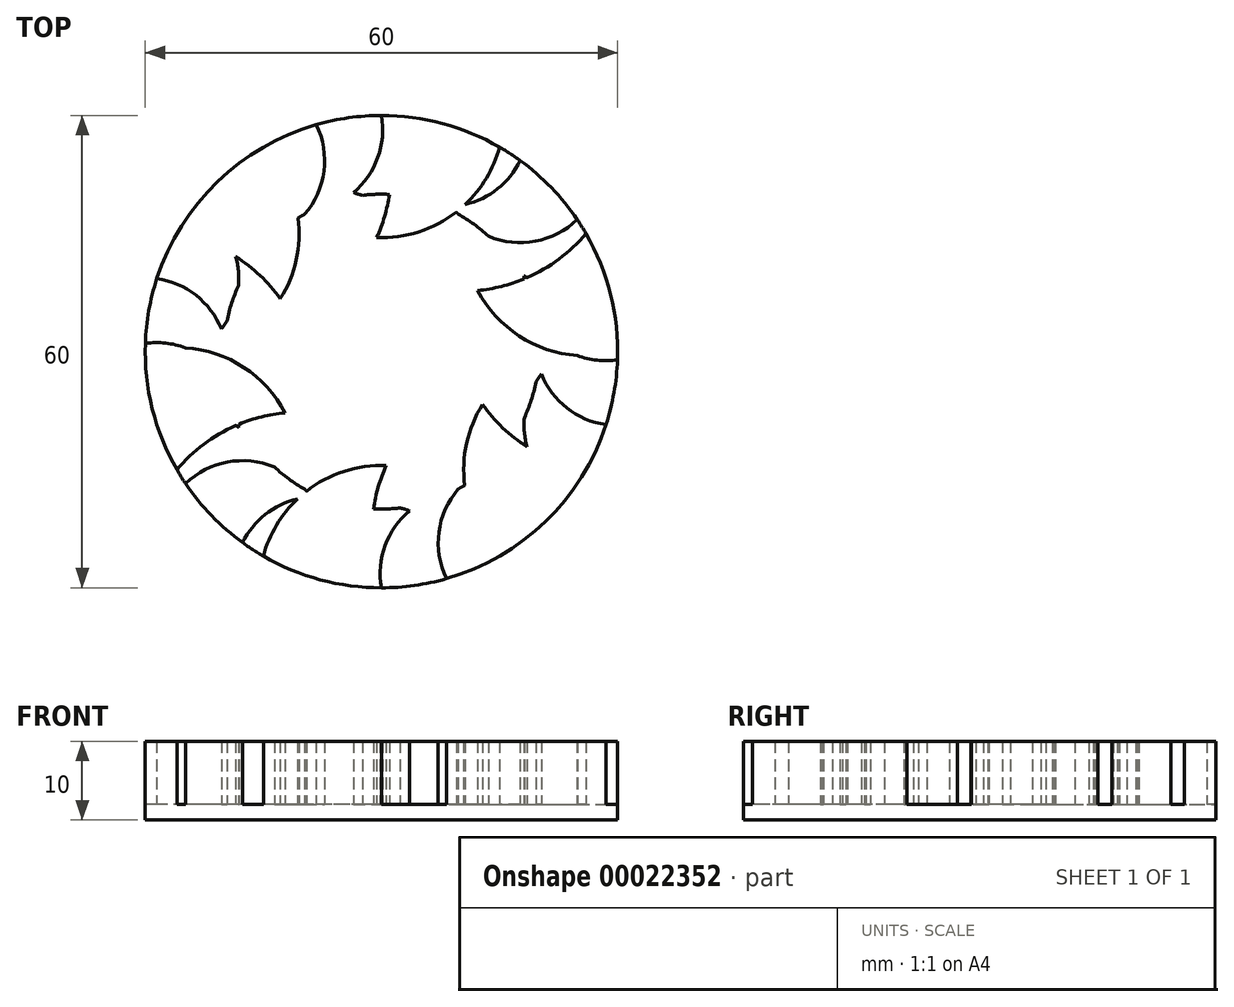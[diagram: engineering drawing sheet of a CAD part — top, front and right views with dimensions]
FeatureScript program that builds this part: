
annotation { "Feature Type Name" : "Feature", "Feature Type Description" : "" }
export const myFeature = defineFeature(function(context is Context, id is Id, definition is map)
    precondition{}
    {
        {
            var Q0;
            Q0=qCreatedBy(makeId("Top.planeOp"),FACE);
            var sketch = newSketch(context, id + "F0", { "sketchPlane" : qUnion([Q0])});
            skCircle(sketch, "E0", {"center": v(0, 0) * mm, "radius": 30 * mm});
            skSolve(sketch);
        }
        {
            var Q0;
            Q0=makeQuery(id+"F0.imprint","IMPRINT",FACE,{"disambiguationData":[TD([[makeQuery(id+"F0.imprint","IMPRINT",EDGE,{"derivedFrom":sQuery(id+"F0.wireOp",EDGE,"E0")}),1.0]])]});
            extrude(context, id + "F1", {"entities" : qUnion([Q0]), "depth" : 2 * mm});
        }
        {
            var Q0;
            Q0=makeQuery(id+"F1.opExtrude","CAP_FACE",FACE,{"disambiguationData":[OSD([sQuery(id+"F0.wireOp",EDGE,"E0")])],"isStart":false});
            var sketch = newSketch(context, id + "F2", { "sketchPlane" : qUnion([Q0])});
            skLineSegment(sketch, "E1", {"start": v(0, 0) * mm, "end": v(0, 30) * mm, "construction": true});
            skLineSegment(sketch, "E2", {"start": v(0, 0) * mm, "end": v(10.26, 28.2) * mm, "construction": true});
            skLineSegment(sketch, "E3", {"start": v(0, 0) * mm, "end": v(-10.26, 28.2) * mm, "construction": true});
            skArc(sketch, "E4", {"start": v(-3.56, 20.2) * mm, "mid": v(5.2, 20.98) * mm, "end": v(10.26, 28.2) * mm});
            skArc(sketch, "E5", {"start": v(-3.56, 20.2) * mm, "mid": v(-0.47, 24.63) * mm, "end": v(0, 30) * mm});
            skArc(sketch, "E6", {"start": v(10.26, 28.2) * mm, "mid": v(5.2, 29.54) * mm, "end": v(0, 30) * mm});
            skSolve(sketch);
        }
        {
            var Q0;
            Q0 = qSketchRegion(id + "F2", true);
            extrude(context, id + "F3", {"entities" : qUnion([Q0]), "operationType" : NewBodyOperationType.ADD, "depth" : 8 * mm});
        }
        {
            var Q0;
            Q0=makeQuery(id+"F1.opExtrude","SWEPT_BODY",BODY,{"disambiguationData":[OSD([sQuery(id+"F0.wireOp",EDGE,"E0")])]});
            var Q1;
            Q1=makeQuery(id+"F1.opExtrude","CAP_EDGE",EDGE,{"disambiguationData":[OSD([sQuery(id+"F0.wireOp",EDGE,"E0")])],"isStart":false});
            var Q2;
            Q2=makeQuery(id+"F1.opExtrude","SWEPT_BODY",BODY,{"disambiguationData":[OSD([sQuery(id+"F0.wireOp",EDGE,"E0")])]});
            circularPattern(context, id + "F4", {"operationType" : NewBodyOperationType.ADD, "entities" : qUnion([Q0]), "axis" : qUnion([Q1]), "angle" : 360 * degree, "instanceCount" : 10, "equalSpace" : true});
        }
        {
            var Q0;
            Q0=sQuery(id+"F0.wireOp",VERTEX,"E0.center");
            var Q1;
            Q1=makeQuery(id+"F1.opExtrude","SWEPT_BODY",BODY,{"disambiguationData":[OSD([sQuery(id+"F0.wireOp",EDGE,"E0")])]});
            hole(context, id + "F5", {"style" : HoleStyle.SIMPLE, "holeDiameter" : 40 * mm, "endStyle" : HoleEndStyle.THROUGH, "oppositeDirection" : true, "locations" : qUnion([Q0]), "scope" : qUnion([Q1])});
        }
        {
            var Q0;
            Q0 = qSketchRegion(id + "F0", true);
            extrude(context, id + "F6", {"entities" : qUnion([Q0]), "depth" : 2 * mm});
        }
        {
            var Q0;
            Q0=makeQuery(id+"F6.opExtrude","CAP_FACE",FACE,{"disambiguationData":[OSD([sQuery(id+"F0.wireOp",EDGE,"E0")])],"isStart":false});
            var sketch = newSketch(context, id + "F7", { "sketchPlane" : qUnion([Q0])});
            skLineSegment(sketch, "E7", {"start": v(0, 0) * mm, "end": v(0, 30) * mm, "construction": true});
            skLineSegment(sketch, "E8", {"start": v(0, 0) * mm, "end": v(15, 25.98) * mm, "construction": true});
            skLineSegment(sketch, "E9", {"start": v(0, 0) * mm, "end": v(-19.28, 22.98) * mm, "construction": true});
            skArc(sketch, "E10", {"start": v(-0.6, 14.48) * mm, "mid": v(1.22, 22.18) * mm, "end": v(0, 30) * mm});
            skArc(sketch, "E11", {"start": v(0, 30) * mm, "mid": v(-39.79, 23.78) * mm, "end": v(-0.6, 14.48) * mm, "construction": true});
            skArc(sketch, "E12", {"start": v(-0.6, 14.48) * mm, "mid": v(9.21, 17.5) * mm, "end": v(15, 25.98) * mm});
            skArc(sketch, "E13", {"start": v(15, 25.98) * mm, "mid": v(-9.21, 42.5) * mm, "end": v(-0.6, 14.48) * mm, "construction": true});
            skArc(sketch, "E14", {"start": v(0, 30) * mm, "mid": v(-7.76, -28.98) * mm, "end": v(15, 25.98) * mm, "construction": true});
            skArc(sketch, "E15", {"start": v(15, 25.98) * mm, "mid": v(7.76, 28.98) * mm, "end": v(0, 30) * mm});
            skArc(sketch, "E16.1.0", {"start": v(-15, 25.98) * mm, "mid": v(-21.21, 21.21) * mm, "end": v(-25.98, 15) * mm});
            skArc(sketch, "E16.1.1", {"start": v(-12.84, 6.72) * mm, "mid": v(-10.55, 16.73) * mm, "end": v(-15, 25.98) * mm});
            skArc(sketch, "E16.1.2", {"start": v(-12.84, 6.72) * mm, "mid": v(-18.6, 12.15) * mm, "end": v(-25.98, 15) * mm});
            skArc(sketch, "E16.2.0", {"start": v(-30, 0) * mm, "mid": v(-28.98, -7.76) * mm, "end": v(-25.98, -15) * mm});
            skArc(sketch, "E16.2.1", {"start": v(-12.24, -7.77) * mm, "mid": v(-19.76, -0.77) * mm, "end": v(-30, 0) * mm});
            skArc(sketch, "E16.2.2", {"start": v(-12.24, -7.77) * mm, "mid": v(-19.82, -10.03) * mm, "end": v(-25.98, -15) * mm});
            skArc(sketch, "E16.3.0", {"start": v(-15, -25.98) * mm, "mid": v(-7.76, -28.98) * mm, "end": v(0, -30) * mm});
            skArc(sketch, "E16.3.1", {"start": v(0.6, -14.48) * mm, "mid": v(-9.21, -17.5) * mm, "end": v(-15, -25.98) * mm});
            skArc(sketch, "E16.3.2", {"start": v(0.6, -14.48) * mm, "mid": v(-1.22, -22.18) * mm, "end": v(0, -30) * mm});
            skArc(sketch, "E16.4.0", {"start": v(15, -25.98) * mm, "mid": v(21.21, -21.21) * mm, "end": v(25.98, -15) * mm});
            skArc(sketch, "E16.4.1", {"start": v(12.84, -6.72) * mm, "mid": v(10.55, -16.73) * mm, "end": v(15, -25.98) * mm});
            skArc(sketch, "E16.4.2", {"start": v(12.84, -6.72) * mm, "mid": v(18.6, -12.15) * mm, "end": v(25.98, -15) * mm});
            skArc(sketch, "E16.5.0", {"start": v(30, 0) * mm, "mid": v(28.98, 7.76) * mm, "end": v(25.98, 15) * mm});
            skArc(sketch, "E16.5.1", {"start": v(12.24, 7.77) * mm, "mid": v(19.76, 0.77) * mm, "end": v(30, 0) * mm});
            skArc(sketch, "E16.5.2", {"start": v(12.24, 7.77) * mm, "mid": v(19.82, 10.03) * mm, "end": v(25.98, 15) * mm});
            skSolve(sketch);
        }
        {
            var Q0;
            Q0 = qSketchRegion(id + "F7", true);
            extrude(context, id + "F8", {"entities" : qUnion([Q0]), "operationType" : NewBodyOperationType.ADD, "depth" : 8 * mm});
        }
    });
